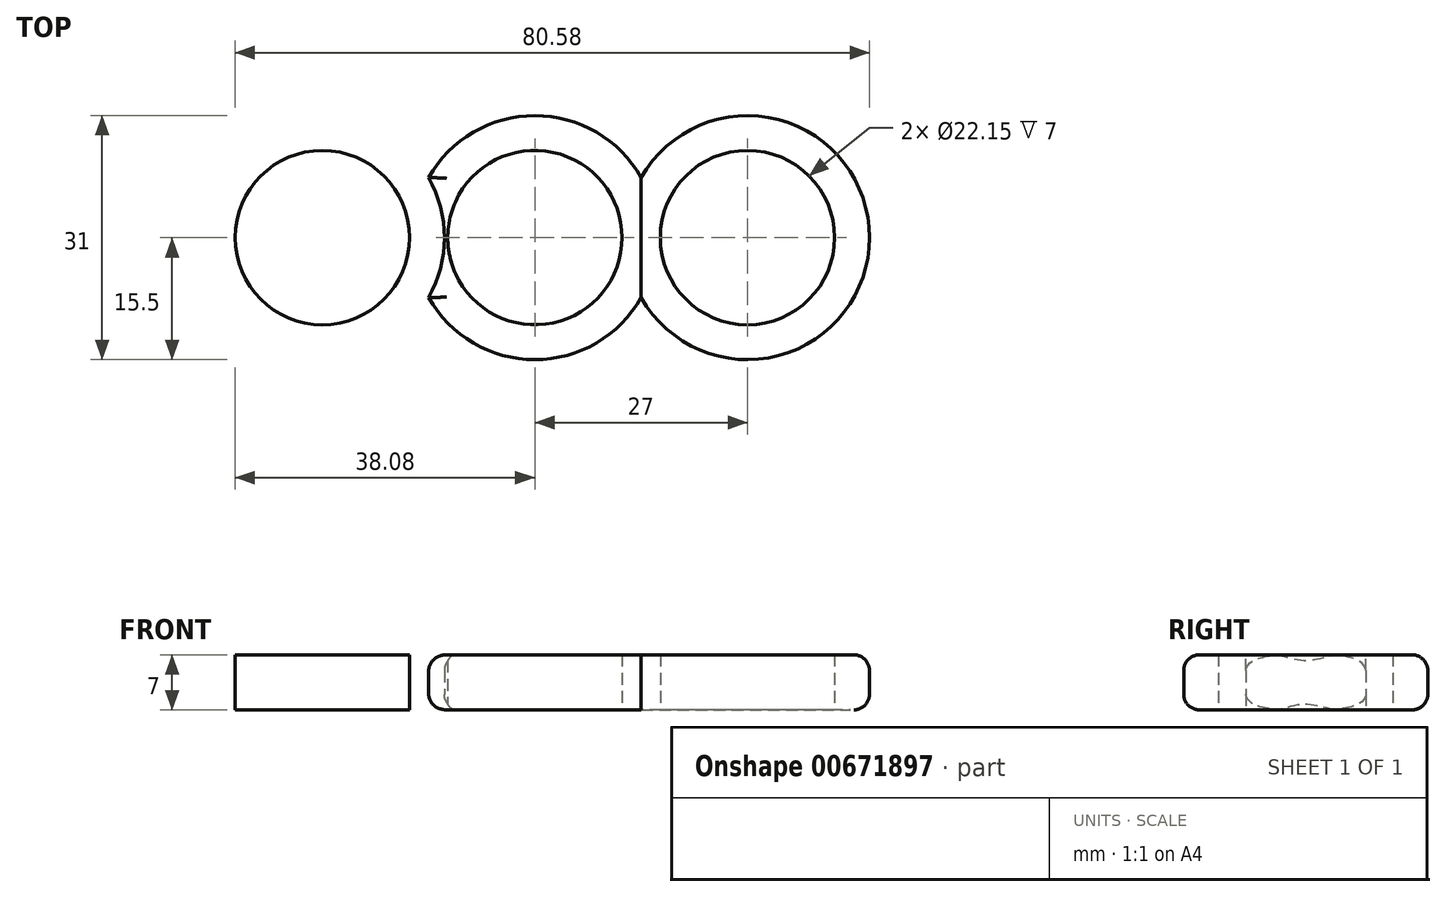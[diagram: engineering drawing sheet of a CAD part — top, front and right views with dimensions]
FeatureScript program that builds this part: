
annotation { "Feature Type Name" : "Feature", "Feature Type Description" : "" }
export const myFeature = defineFeature(function(context is Context, id is Id, definition is map)
    precondition{}
    {
        {
            var Q0;
            Q0=qCreatedBy(makeId("Top.planeOp"),FACE);
            var sketch = newSketch(context, id + "F0", { "sketchPlane" : qUnion([Q0])});
            skCircle(sketch, "E0", {"center": v(0, 0) * mm, "radius": 11.07 * mm});
            skLineSegment(sketch, "E1", {"start": v(0, 0) * mm, "end": v(27, 0) * mm, "construction": true});
            skCircle(sketch, "E2", {"center": v(27, 0) * mm, "radius": 11.07 * mm});
            skCircle(sketch, "E3", {"center": v(27, 0) * mm, "radius": 15.5 * mm});
            skLineSegment(sketch, "E4", {"start": v(0, 35.6) * mm, "end": v(0, -42.11) * mm, "construction": true});
            skLineSegment(sketch, "E5", {"start": v(0, 11.07) * mm, "end": v(0, -11.07) * mm});
            skCircle(sketch, "E6.MirrorC", {"center": v(-27, 0) * mm, "radius": 11.07 * mm});
            skCircle(sketch, "E7.MirrorC", {"center": v(-27, 0) * mm, "radius": 15.5 * mm});
            skCircle(sketch, "E8", {"center": v(0, 0) * mm, "radius": 15.5 * mm});
            skSolve(sketch);
        }
        {
            var Q0;
            Q0=makeQuery(id+"F0.imprint","IMPRINT",FACE,{"disambiguationData":[TD([[makeQuery(id+"F0.imprint","IMPRINT",EDGE,{"derivedFrom":sQuery(id+"F0.wireOp",EDGE,"E6.MirrorC")}),1.0]])]});
            var Q1;
            {var subQ0=sQuery(id+"F0.wireOp",EDGE,"E8");var subQ1=sQuery(id+"F0.wireOp",EDGE,"E7.MirrorC");var subQ2=makeQuery(id+"F0.imprint","INTERSECT",VERTEX,{"disambiguationData":[OD(0.0)],"derivedFrom":[subQ1,subQ0]});Q1=makeQuery(id+"F0.imprint","IMPRINT",FACE,{"disambiguationData":[TD([[makeQuery(id+"F0.imprint","IMPRINT",EDGE,{"disambiguationData":[TD([[subQ2,-1.0]])],"derivedFrom":subQ1}),-1.0]])]});}
            var Q2;
            {var subQ7=sQuery(id+"F0.wireOp",EDGE,"E5");var subQ8=sQuery(id+"F0.wireOp",EDGE,"E0");var subQ9=makeQuery(id+"F0.imprint","INTERSECT",VERTEX,{"disambiguationData":[OD(0.0)],"derivedFrom":[subQ8,subQ7]});Q2=makeQuery(id+"F0.imprint","IMPRINT",FACE,{"disambiguationData":[TD([[makeQuery(id+"F0.imprint","IMPRINT",EDGE,{"disambiguationData":[TD([[subQ9,-1.0]])],"derivedFrom":subQ8}),-1.0]])]});}
            var Q3;
            Q3=makeQuery(id+"F0.imprint","IMPRINT",FACE,{"disambiguationData":[TD([[makeQuery(id+"F0.imprint","IMPRINT",EDGE,{"derivedFrom":sQuery(id+"F0.wireOp",EDGE,"E2")}),-1.0]])]});
            var Q4;
            {var subQ0=sQuery(id+"F0.wireOp",EDGE,"E8");var subQ1=sQuery(id+"F0.wireOp",EDGE,"E3");var subQ2=makeQuery(id+"F0.imprint","INTERSECT",VERTEX,{"disambiguationData":[OD(0.0)],"derivedFrom":[subQ1,subQ0]});Q4=makeQuery(id+"F0.imprint","IMPRINT",FACE,{"disambiguationData":[TD([[makeQuery(id+"F0.imprint","IMPRINT",EDGE,{"disambiguationData":[TD([[subQ2,-1.0]])],"derivedFrom":subQ1}),1.0]])]});}
            extrude(context, id + "F1", {"entities" : qUnion([Q0, Q1, Q2, Q3, Q4]), "depth" : 7 * mm, "offsetDistance" : 25 * mm});
        }
        {
            var Q0;
            Q0=makeQuery(id+"F1.opExtrude","CAP_EDGE",EDGE,{"disambiguationData":[OSD([sQuery(id+"F0.wireOp",EDGE,"E7.MirrorC")])],"isStart":false});
            var Q1;
            {var subQ0=sQuery(id+"F0.wireOp",EDGE,"E8");Q1=makeQuery(id+"F1.opExtrude","CAP_EDGE",EDGE,{"disambiguationData":[OSD([subQ0]),TDD([makeQuery(id+"F0.imprint","IMPRINT",EDGE,{"disambiguationData":[TD([[makeQuery(id+"F0.imprint","INTERSECT",VERTEX,{"disambiguationData":[OD(1.0)],"derivedFrom":[sQuery(id+"F0.wireOp",EDGE,"E3"),subQ0]}),1.0]])],"derivedFrom":subQ0})])],"isStart":false});}
            var Q2;
            Q2=makeQuery(id+"F1.opExtrude","CAP_EDGE",EDGE,{"disambiguationData":[OSD([sQuery(id+"F0.wireOp",EDGE,"E3")])],"isStart":false});
            var Q3;
            {var subQ0=sQuery(id+"F0.wireOp",EDGE,"E8");Q3=makeQuery(id+"F1.opExtrude","CAP_EDGE",EDGE,{"disambiguationData":[OSD([subQ0]),TDD([makeQuery(id+"F0.imprint","IMPRINT",EDGE,{"disambiguationData":[TD([[makeQuery(id+"F0.imprint","INTERSECT",VERTEX,{"disambiguationData":[OD(0.0)],"derivedFrom":[sQuery(id+"F0.wireOp",EDGE,"E3"),subQ0]}),-1.0]])],"derivedFrom":subQ0})])],"isStart":false});}
            var Q4;
            Q4=makeQuery(id+"F1.opExtrude","CAP_EDGE",EDGE,{"disambiguationData":[OSD([sQuery(id+"F0.wireOp",EDGE,"E7.MirrorC")])],"isStart":true});
            var Q5;
            {var subQ0=sQuery(id+"F0.wireOp",EDGE,"E8");Q5=makeQuery(id+"F1.opExtrude","CAP_EDGE",EDGE,{"disambiguationData":[OSD([subQ0]),TDD([makeQuery(id+"F0.imprint","IMPRINT",EDGE,{"disambiguationData":[TD([[makeQuery(id+"F0.imprint","INTERSECT",VERTEX,{"disambiguationData":[OD(1.0)],"derivedFrom":[sQuery(id+"F0.wireOp",EDGE,"E3"),subQ0]}),1.0]])],"derivedFrom":subQ0})])],"isStart":true});}
            var Q6;
            {var subQ0=sQuery(id+"F0.wireOp",EDGE,"E8");Q6=makeQuery(id+"F1.opExtrude","CAP_EDGE",EDGE,{"disambiguationData":[OSD([subQ0]),TDD([makeQuery(id+"F0.imprint","IMPRINT",EDGE,{"disambiguationData":[TD([[makeQuery(id+"F0.imprint","INTERSECT",VERTEX,{"disambiguationData":[OD(0.0)],"derivedFrom":[sQuery(id+"F0.wireOp",EDGE,"E3"),subQ0]}),-1.0]])],"derivedFrom":subQ0})])],"isStart":true});}
            var Q7;
            Q7=makeQuery(id+"F1.opExtrude","CAP_EDGE",EDGE,{"disambiguationData":[OSD([sQuery(id+"F0.wireOp",EDGE,"E3")])],"isStart":true});
            fillet(context, id + "F2", {"entities" : qUnion([Q0, Q1, Q2, Q3, Q4, Q5, Q6, Q7]), "radius" : 2 * mm, "tangentPropagation" : true, "allowEdgeOverflow" : false});
        }
    });
